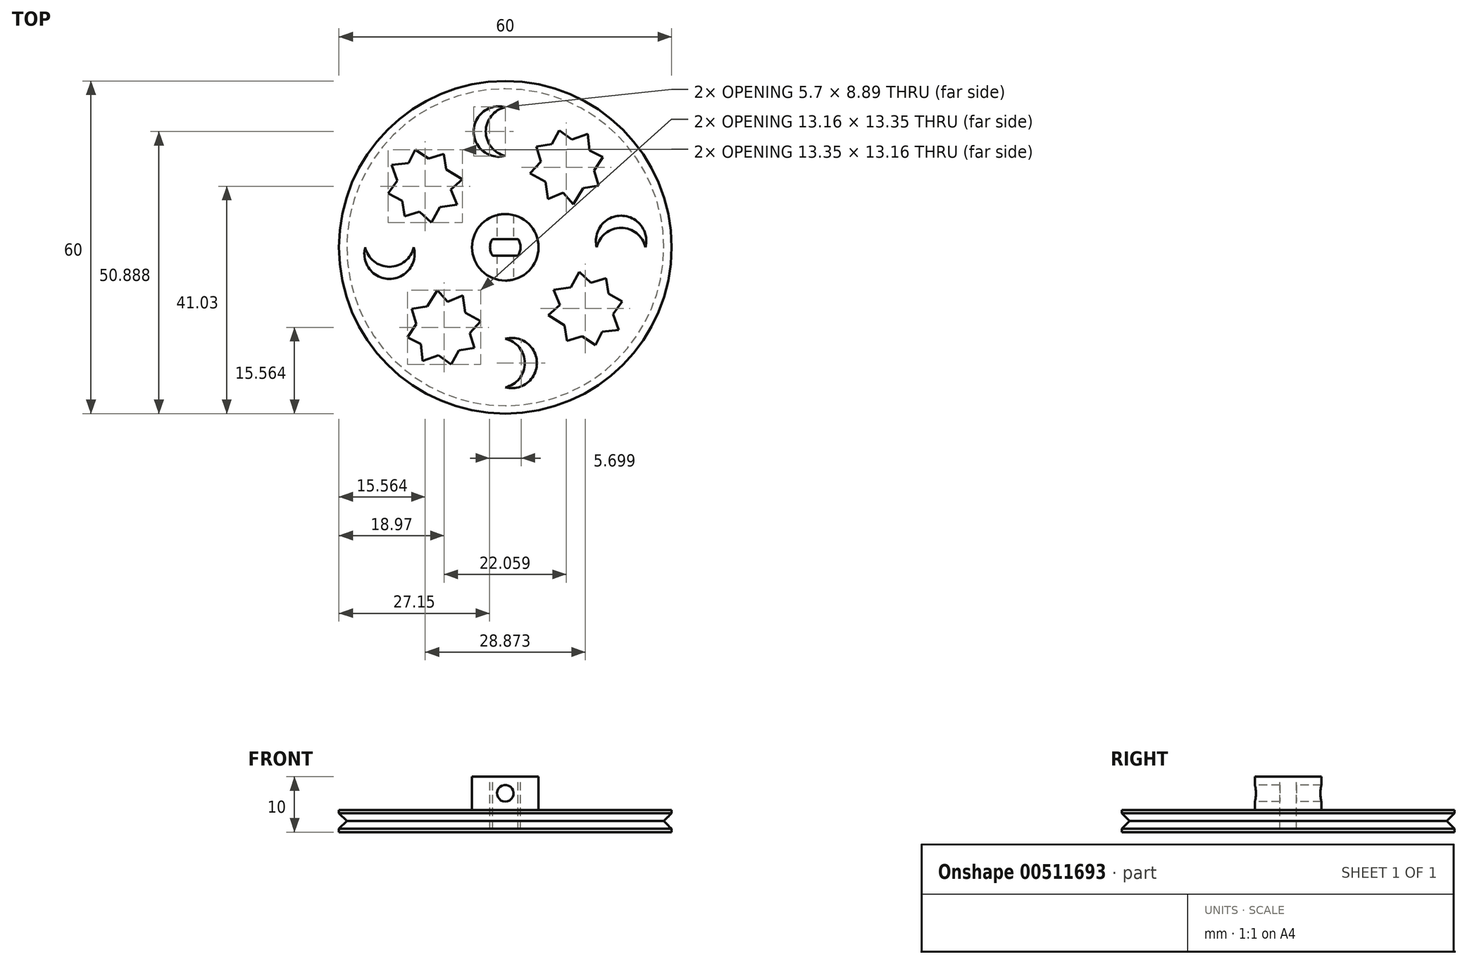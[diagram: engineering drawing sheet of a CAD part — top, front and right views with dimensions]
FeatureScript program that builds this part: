
annotation { "Feature Type Name" : "Feature", "Feature Type Description" : "" }
export const myFeature = defineFeature(function(context is Context, id is Id, definition is map)
    precondition{}
    {
        {
            var Q0;
            Q0=qCreatedBy(makeId("Top.planeOp"),FACE);
            var sketch = newSketch(context, id + "F0", { "sketchPlane" : qUnion([Q0])});
            skCircle(sketch, "E0", {"center": v(0, 0) * mm, "radius": 30 * mm});
            skSolve(sketch);
        }
        {
            var Q0;
            Q0 = qSketchRegion(id + "F0", true);
            extrude(context, id + "F1", {"entities" : qUnion([Q0]), "depth" : 4 * mm, "offsetDistance" : 25 * mm});
        }
        {
            var Q0;
            Q0=makeQuery(id+"F1.opExtrude","CAP_FACE",FACE,{"disambiguationData":[OSD([sQuery(id+"F0.wireOp",EDGE,"E0")])],"isStart":false});
            var sketch = newSketch(context, id + "F2", { "sketchPlane" : qUnion([Q0])});
            skCircle(sketch, "E1", {"center": v(0, 0) * mm, "radius": 6 * mm});
            skSolve(sketch);
        }
        {
            var Q0;
            Q0 = qSketchRegion(id + "F2", true);
            extrude(context, id + "F3", {"entities" : qUnion([Q0]), "operationType" : NewBodyOperationType.ADD, "depth" : 6 * mm, "offsetDistance" : 25 * mm});
        }
        {
            var Q0;
            Q0=qCreatedBy(makeId("Front.planeOp"),FACE);
            var sketch = newSketch(context, id + "F4", { "sketchPlane" : qUnion([Q0])});
            skCircle(sketch, "E2", {"center": v(0, 7) * mm, "radius": 1.5 * mm});
            skSolve(sketch);
        }
        {
            var Q0;
            Q0 = qSketchRegion(id + "F4", true);
            extrude(context, id + "F5", {"entities" : qUnion([Q0]), "operationType" : NewBodyOperationType.REMOVE, "endBound" : BoundingType.SYMMETRIC, "oppositeDirection" : true, "depth" : 19.9 * mm, "offsetDistance" : 25 * mm});
        }
        {
            var Q0;
            Q0=makeQuery(id+"F3.opExtrude","CAP_FACE",FACE,{"disambiguationData":[OSD([sQuery(id+"F2.wireOp",EDGE,"E1")])],"isStart":false});
            var sketch = newSketch(context, id + "F6", { "sketchPlane" : qUnion([Q0])});
            skLineSegment(sketch, "E3.bottom", {"start": v(2.3, 1.5) * mm, "end": v(-2.3, 1.5) * mm});
            skLineSegment(sketch, "E3.top", {"start": v(2.3, -1.5) * mm, "end": v(-2.3, -1.5) * mm});
            skLineSegment(sketch, "E3.left", {"start": v(2.3, 1.5) * mm, "end": v(2.3, -1.5) * mm});
            skLineSegment(sketch, "E3.right", {"start": v(-2.3, 1.5) * mm, "end": v(-2.3, -1.5) * mm});
            skPoint(sketch, "E3.middle", {"position": v(0, 0) * mm});
            skArc(sketch, "E4", {"start": v(2.3, -1.5) * mm, "mid": v(2.75, 0) * mm, "end": v(2.3, 1.5) * mm});
            skArc(sketch, "E5", {"start": v(-2.3, 1.5) * mm, "mid": v(-2.75, 0) * mm, "end": v(-2.3, -1.5) * mm});
            skLineSegment(sketch, "E6", {"start": v(-2.75, 0) * mm, "end": v(2.75, 0) * mm, "construction": true});
            skSolve(sketch);
        }
        {
            var Q0;
            Q0 = qSketchRegion(id + "F6", true);
            extrude(context, id + "F7", {"entities" : qUnion([Q0]), "operationType" : NewBodyOperationType.REMOVE, "oppositeDirection" : true, "depth" : 9.4 * mm, "offsetDistance" : 25 * mm});
        }
        {
            var Q0;
            Q0=makeQuery(id+"F1.opExtrude","CAP_FACE",FACE,{"disambiguationData":[OSD([sQuery(id+"F0.wireOp",EDGE,"E0")])],"isStart":false});
            var sketch = newSketch(context, id + "F8", { "sketchPlane" : qUnion([Q0])});
            skArc(sketch, "E7", {"start": v(0, 25.27) * mm, "mid": v(-5.7, 20.89) * mm, "end": v(0, 16.5) * mm});
            skArc(sketch, "E8", {"start": v(0, 25.27) * mm, "mid": v(-3.51, 20.89) * mm, "end": v(0, 16.5) * mm});
            skArc(sketch, "E9.1.0", {"start": v(-25.27, 0) * mm, "mid": v(-20.89, -3.51) * mm, "end": v(-16.5, 0) * mm});
            skArc(sketch, "E9.1.1", {"start": v(-25.27, 0) * mm, "mid": v(-20.89, -5.7) * mm, "end": v(-16.5, 0) * mm});
            skArc(sketch, "E9.2.0", {"start": v(0, -25.27) * mm, "mid": v(3.51, -20.89) * mm, "end": v(0, -16.5) * mm});
            skArc(sketch, "E9.2.1", {"start": v(0, -25.27) * mm, "mid": v(5.7, -20.89) * mm, "end": v(0, -16.5) * mm});
            skArc(sketch, "E9.3.0", {"start": v(25.27, 0) * mm, "mid": v(20.89, 3.51) * mm, "end": v(16.5, 0) * mm});
            skArc(sketch, "E9.3.1", {"start": v(25.27, 0) * mm, "mid": v(20.89, 5.7) * mm, "end": v(16.5, 0) * mm});
            skPoint(sketch, "E9.center", {"position": v(0, 0) * mm});
            skSolve(sketch);
        }
        {
            var Q0;
            Q0 = qSketchRegion(id + "F8", true);
            extrude(context, id + "F9", {"entities" : qUnion([Q0]), "operationType" : NewBodyOperationType.REMOVE, "oppositeDirection" : true, "depth" : 25 * mm, "offsetDistance" : 25 * mm});
        }
        {
            var Q0;
            Q0=makeQuery(id+"F1.opExtrude","CAP_FACE",FACE,{"disambiguationData":[OSD([sQuery(id+"F0.wireOp",EDGE,"E0")])],"isStart":false});
            var sketch = newSketch(context, id + "F10", { "sketchPlane" : qUnion([Q0])});
            skPoint(sketch, "E10", {"position": v(-14.65, 11.23) * mm});
            skCircle(sketch, "E11.cCircle", {"center": v(-14.65, 11.23) * mm, "radius": 4.88 * mm});
            skLineSegment(sketch, "E11.0", {"start": v(-19.46, 12.04) * mm, "end": v(-17.48, 15.21) * mm});
            skLineSegment(sketch, "E11.1", {"start": v(-17.48, 15.21) * mm, "end": v(-13.83, 16.05) * mm});
            skLineSegment(sketch, "E11.2", {"start": v(-13.83, 16.05) * mm, "end": v(-10.67, 14.06) * mm});
            skLineSegment(sketch, "E11.3", {"start": v(-10.67, 14.06) * mm, "end": v(-9.83, 10.42) * mm});
            skLineSegment(sketch, "E11.4", {"start": v(-9.83, 10.42) * mm, "end": v(-11.81, 7.25) * mm});
            skLineSegment(sketch, "E11.5", {"start": v(-11.81, 7.25) * mm, "end": v(-15.46, 6.42) * mm});
            skLineSegment(sketch, "E11.6", {"start": v(-15.46, 6.42) * mm, "end": v(-18.62, 8.4) * mm});
            skLineSegment(sketch, "E11.7", {"start": v(-18.62, 8.4) * mm, "end": v(-19.46, 12.04) * mm});
            skLineSegment(sketch, "E12", {"start": v(-18.47, 13.63) * mm, "end": v(-10.82, 8.83) * mm, "construction": true});
            skLineSegment(sketch, "E13", {"start": v(-17.04, 7.4) * mm, "end": v(-12.25, 15.05) * mm, "construction": true});
            skLineSegment(sketch, "E14", {"start": v(-19.04, 10.22) * mm, "end": v(-10.25, 12.24) * mm, "construction": true});
            skLineSegment(sketch, "E15", {"start": v(-15.65, 15.63) * mm, "end": v(-13.64, 6.83) * mm, "construction": true});
            skLineSegment(sketch, "E16", {"start": v(-18.47, 13.63) * mm, "end": v(-22.47, 16.13) * mm, "construction": true});
            skLineSegment(sketch, "E17", {"start": v(-19.46, 12.04) * mm, "end": v(-20.47, 14.88) * mm});
            skLineSegment(sketch, "E18", {"start": v(-20.47, 14.88) * mm, "end": v(-17.48, 15.21) * mm});
            skLineSegment(sketch, "E19", {"start": v(-15.65, 15.63) * mm, "end": v(-16.84, 19.6) * mm, "construction": true});
            skLineSegment(sketch, "E20", {"start": v(-12.25, 15.05) * mm, "end": v(-9.88, 18.84) * mm, "construction": true});
            skLineSegment(sketch, "E21", {"start": v(-10.25, 12.24) * mm, "end": v(-6.79, 12.24) * mm, "construction": true});
            skLineSegment(sketch, "E22", {"start": v(-10.82, 8.83) * mm, "end": v(-7.9, 7.25) * mm, "construction": true});
            skLineSegment(sketch, "E23", {"start": v(-13.64, 6.83) * mm, "end": v(-13.17, 3.24) * mm, "construction": true});
            skLineSegment(sketch, "E24", {"start": v(-17.04, 7.4) * mm, "end": v(-19.08, 4.15) * mm, "construction": true});
            skLineSegment(sketch, "E25", {"start": v(-19.04, 10.22) * mm, "end": v(-23.29, 9.25) * mm, "construction": true});
            skLineSegment(sketch, "E26", {"start": v(-17.48, 15.21) * mm, "end": v(-16.25, 17.6) * mm});
            skLineSegment(sketch, "E27", {"start": v(-16.25, 17.6) * mm, "end": v(-13.83, 16.05) * mm});
            skLineSegment(sketch, "E28", {"start": v(-13.83, 16.05) * mm, "end": v(-11.12, 16.86) * mm});
            skLineSegment(sketch, "E29", {"start": v(-11.12, 16.86) * mm, "end": v(-10.67, 14.06) * mm});
            skLineSegment(sketch, "E30", {"start": v(-10.67, 14.06) * mm, "end": v(-7.76, 12.24) * mm});
            skLineSegment(sketch, "E31", {"start": v(-7.76, 12.24) * mm, "end": v(-9.83, 10.42) * mm});
            skLineSegment(sketch, "E32", {"start": v(-9.83, 10.42) * mm, "end": v(-8.69, 7.68) * mm});
            skLineSegment(sketch, "E33", {"start": v(-8.69, 7.68) * mm, "end": v(-11.81, 7.25) * mm});
            skLineSegment(sketch, "E34", {"start": v(-11.81, 7.25) * mm, "end": v(-13.33, 4.45) * mm});
            skLineSegment(sketch, "E35", {"start": v(-13.33, 4.45) * mm, "end": v(-15.46, 6.42) * mm});
            skLineSegment(sketch, "E36", {"start": v(-15.46, 6.42) * mm, "end": v(-18.17, 5.6) * mm});
            skLineSegment(sketch, "E37", {"start": v(-18.17, 5.6) * mm, "end": v(-18.62, 8.4) * mm});
            skLineSegment(sketch, "E38", {"start": v(-18.62, 8.4) * mm, "end": v(-21.11, 9.75) * mm});
            skLineSegment(sketch, "E39", {"start": v(-19.46, 12.04) * mm, "end": v(-21.11, 9.75) * mm});
            skLineSegment(sketch, "E40.1.0", {"start": v(-12.04, -19.46) * mm, "end": v(-14.88, -20.47) * mm});
            skLineSegment(sketch, "E40.1.1", {"start": v(-14.88, -20.47) * mm, "end": v(-15.21, -17.48) * mm});
            skLineSegment(sketch, "E40.1.2", {"start": v(-15.21, -17.48) * mm, "end": v(-17.6, -16.25) * mm});
            skLineSegment(sketch, "E40.1.3", {"start": v(-17.6, -16.25) * mm, "end": v(-16.05, -13.83) * mm});
            skLineSegment(sketch, "E40.1.4", {"start": v(-16.05, -13.83) * mm, "end": v(-16.86, -11.12) * mm});
            skLineSegment(sketch, "E40.1.5", {"start": v(-16.86, -11.12) * mm, "end": v(-14.06, -10.67) * mm});
            skLineSegment(sketch, "E40.1.6", {"start": v(-14.06, -10.67) * mm, "end": v(-12.24, -7.76) * mm});
            skLineSegment(sketch, "E40.1.7", {"start": v(-12.24, -7.76) * mm, "end": v(-10.42, -9.83) * mm});
            skLineSegment(sketch, "E40.1.8", {"start": v(-10.42, -9.83) * mm, "end": v(-7.68, -8.69) * mm});
            skLineSegment(sketch, "E40.1.9", {"start": v(-7.68, -8.69) * mm, "end": v(-7.25, -11.81) * mm});
            skLineSegment(sketch, "E40.1.10", {"start": v(-7.25, -11.81) * mm, "end": v(-4.45, -13.33) * mm});
            skLineSegment(sketch, "E40.1.11", {"start": v(-4.45, -13.33) * mm, "end": v(-6.42, -15.46) * mm});
            skLineSegment(sketch, "E40.1.12", {"start": v(-6.42, -15.46) * mm, "end": v(-5.6, -18.17) * mm});
            skLineSegment(sketch, "E40.1.13", {"start": v(-5.6, -18.17) * mm, "end": v(-8.4, -18.62) * mm});
            skLineSegment(sketch, "E40.1.14", {"start": v(-8.4, -18.62) * mm, "end": v(-9.75, -21.11) * mm});
            skLineSegment(sketch, "E40.1.15", {"start": v(-12.04, -19.46) * mm, "end": v(-9.75, -21.11) * mm});
            skLineSegment(sketch, "E40.2.0", {"start": v(19.46, -12.04) * mm, "end": v(20.47, -14.88) * mm});
            skLineSegment(sketch, "E40.2.1", {"start": v(20.47, -14.88) * mm, "end": v(17.48, -15.21) * mm});
            skLineSegment(sketch, "E40.2.2", {"start": v(17.48, -15.21) * mm, "end": v(16.25, -17.6) * mm});
            skLineSegment(sketch, "E40.2.3", {"start": v(16.25, -17.6) * mm, "end": v(13.83, -16.05) * mm});
            skLineSegment(sketch, "E40.2.4", {"start": v(13.83, -16.05) * mm, "end": v(11.12, -16.86) * mm});
            skLineSegment(sketch, "E40.2.5", {"start": v(11.12, -16.86) * mm, "end": v(10.67, -14.06) * mm});
            skLineSegment(sketch, "E40.2.6", {"start": v(10.67, -14.06) * mm, "end": v(7.76, -12.24) * mm});
            skLineSegment(sketch, "E40.2.7", {"start": v(7.76, -12.24) * mm, "end": v(9.83, -10.42) * mm});
            skLineSegment(sketch, "E40.2.8", {"start": v(9.83, -10.42) * mm, "end": v(8.69, -7.68) * mm});
            skLineSegment(sketch, "E40.2.9", {"start": v(8.69, -7.68) * mm, "end": v(11.81, -7.25) * mm});
            skLineSegment(sketch, "E40.2.10", {"start": v(11.81, -7.25) * mm, "end": v(13.33, -4.45) * mm});
            skLineSegment(sketch, "E40.2.11", {"start": v(13.33, -4.45) * mm, "end": v(15.46, -6.42) * mm});
            skLineSegment(sketch, "E40.2.12", {"start": v(15.46, -6.42) * mm, "end": v(18.17, -5.6) * mm});
            skLineSegment(sketch, "E40.2.13", {"start": v(18.17, -5.6) * mm, "end": v(18.62, -8.4) * mm});
            skLineSegment(sketch, "E40.2.14", {"start": v(18.62, -8.4) * mm, "end": v(21.11, -9.75) * mm});
            skLineSegment(sketch, "E40.2.15", {"start": v(19.46, -12.04) * mm, "end": v(21.11, -9.75) * mm});
            skLineSegment(sketch, "E40.3.0", {"start": v(12.04, 19.46) * mm, "end": v(14.88, 20.47) * mm});
            skLineSegment(sketch, "E40.3.1", {"start": v(14.88, 20.47) * mm, "end": v(15.21, 17.48) * mm});
            skLineSegment(sketch, "E40.3.2", {"start": v(15.21, 17.48) * mm, "end": v(17.6, 16.25) * mm});
            skLineSegment(sketch, "E40.3.3", {"start": v(17.6, 16.25) * mm, "end": v(16.05, 13.83) * mm});
            skLineSegment(sketch, "E40.3.4", {"start": v(16.05, 13.83) * mm, "end": v(16.86, 11.12) * mm});
            skLineSegment(sketch, "E40.3.5", {"start": v(16.86, 11.12) * mm, "end": v(14.06, 10.67) * mm});
            skLineSegment(sketch, "E40.3.6", {"start": v(14.06, 10.67) * mm, "end": v(12.24, 7.76) * mm});
            skLineSegment(sketch, "E40.3.7", {"start": v(12.24, 7.76) * mm, "end": v(10.42, 9.83) * mm});
            skLineSegment(sketch, "E40.3.8", {"start": v(10.42, 9.83) * mm, "end": v(7.68, 8.69) * mm});
            skLineSegment(sketch, "E40.3.9", {"start": v(7.68, 8.69) * mm, "end": v(7.25, 11.81) * mm});
            skLineSegment(sketch, "E40.3.10", {"start": v(7.25, 11.81) * mm, "end": v(4.45, 13.33) * mm});
            skLineSegment(sketch, "E40.3.11", {"start": v(4.45, 13.33) * mm, "end": v(6.42, 15.46) * mm});
            skLineSegment(sketch, "E40.3.12", {"start": v(6.42, 15.46) * mm, "end": v(5.6, 18.17) * mm});
            skLineSegment(sketch, "E40.3.13", {"start": v(5.6, 18.17) * mm, "end": v(8.4, 18.62) * mm});
            skLineSegment(sketch, "E40.3.14", {"start": v(8.4, 18.62) * mm, "end": v(9.75, 21.11) * mm});
            skLineSegment(sketch, "E40.3.15", {"start": v(12.04, 19.46) * mm, "end": v(9.75, 21.11) * mm});
            skPoint(sketch, "E40.center", {"position": v(0, 0) * mm});
            skSolve(sketch);
        }
        {
            var Q0;
            Q0 = qSketchRegion(id + "F10", true);
            extrude(context, id + "F11", {"entities" : qUnion([Q0]), "operationType" : NewBodyOperationType.REMOVE, "oppositeDirection" : true, "depth" : 25 * mm, "offsetDistance" : 25 * mm});
        }
        {
            var Q0;
            Q0=qCreatedBy(makeId("Front.planeOp"),FACE);
            var sketch = newSketch(context, id + "F12", { "sketchPlane" : qUnion([Q0])});
            skLineSegment(sketch, "E41", {"start": v(30, 3.41) * mm, "end": v(30, 0.59) * mm});
            skLineSegment(sketch, "E42", {"start": v(30, 3.41) * mm, "end": v(28.59, 2) * mm});
            skLineSegment(sketch, "E43", {"start": v(28.59, 2) * mm, "end": v(30, 0.59) * mm});
            skLineSegment(sketch, "E44", {"start": v(30, 4) * mm, "end": v(30, 0) * mm, "construction": true});
            skLineSegment(sketch, "E45", {"start": v(30, 2) * mm, "end": v(27.9, 2) * mm, "construction": true});
            skLineSegment(sketch, "E46", {"start": v(0, -4.86) * mm, "end": v(0, 11.67) * mm, "construction": true});
            skSolve(sketch);
        }
        {
            var Q0;
            Q0 = qSketchRegion(id + "F12", true);
            var Q1;
            Q1=sQuery(id+"F12.wireOp",EDGE,"E46");
            revolve(context, id + "F13", {"operationType" : NewBodyOperationType.REMOVE, "surfaceOperationType" : NewSurfaceOperationType.NEW, "entities" : qUnion([Q0]), "axis" : qUnion([Q1]), "revolveType" : RevolveType.FULL, "oppositeDirection" : true});
        }
    });
